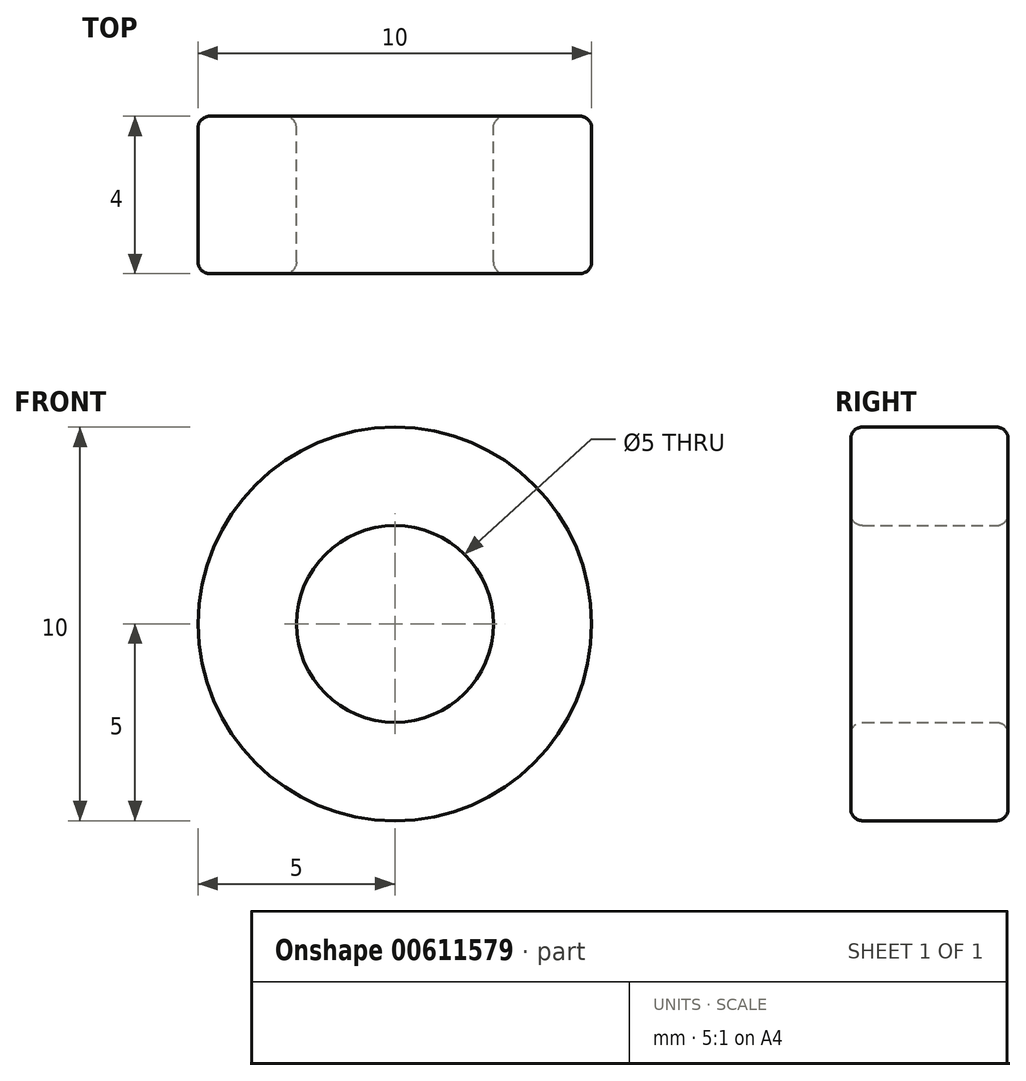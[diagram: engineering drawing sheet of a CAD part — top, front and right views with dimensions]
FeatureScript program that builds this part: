
annotation { "Feature Type Name" : "Feature", "Feature Type Description" : "" }
export const myFeature = defineFeature(function(context is Context, id is Id, definition is map)
    precondition{}
    {
        {
            var Q0;
            Q0=qCreatedBy(makeId("Front.planeOp"),FACE);
            var sketch = newSketch(context, id + "F0", { "sketchPlane" : qUnion([Q0])});
            skCircle(sketch, "E0", {"center": v(0, 0) * mm, "radius": 2.5 * mm});
            skCircle(sketch, "E1", {"center": v(0, 0) * mm, "radius": 5 * mm});
            skSolve(sketch);
        }
        {
            var Q0;
            Q0 = qSketchRegion(id + "F0", true);
            extrude(context, id + "F1", {"entities" : qUnion([Q0]), "endBound" : BoundingType.SYMMETRIC, "depth" : 4 * mm, "offsetDistance" : 25 * mm});
        }
        {
            var Q0;
            Q0=makeQuery(id+"F1.opExtrude","SWEPT_FACE",FACE,{"disambiguationData":[OSD([sQuery(id+"F0.wireOp",EDGE,"E1")])]});
            var Q1;
            Q1=makeQuery(id+"F1.opExtrude","SWEPT_FACE",FACE,{"disambiguationData":[OSD([sQuery(id+"F0.wireOp",EDGE,"E0")])]});
            fillet(context, id + "F2", {"entities" : qUnion([Q0, Q1]), "radius" : 0.3 * mm, "tangentPropagation" : true, "allowEdgeOverflow" : false});
        }
    });
